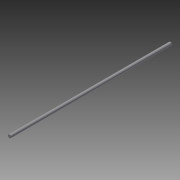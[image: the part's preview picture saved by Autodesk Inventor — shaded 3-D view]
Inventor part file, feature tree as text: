
AUTODESK INVENTOR PART (.ipt)
format: ipt  version: 2015 (Build 190159000, 159)  size: 64,512 bytes
history: native  units: in
note: dims shown in document units (in); Inventor stores cm internally (conversion verified against a paired STEP export)
features: extrude x1, sketch x1
ambient origin geometry x8: Origin, YZ Plane, XZ Plane, XY Plane, X Axis, Y Axis, Z Axis, Center Point
bodies: Solid1 (feature_tree)
feature tree (2):
  extrude  "Extrusion1"  Depth=13.0in TaperAngle=0.0deg
  sketch  "Sketch1"  dims[d0=0.25in d1=13.0in d2=0.0in]
